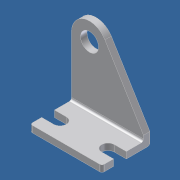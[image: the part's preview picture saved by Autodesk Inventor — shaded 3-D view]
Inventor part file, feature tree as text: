
AUTODESK INVENTOR PART (.ipt)
format: ipt  version: unknown  size: 245,760 bytes
history: native  units: in
note: dims shown in document units (in); Inventor stores cm internally (conversion verified against a paired STEP export)
features: other x147, extrude x8, sketch x8
ambient origin geometry x8: Origin, YZ Plane, XZ Plane, XY Plane, X Axis, Y Axis, Z Axis, Center Point
feature tree (163):
  extrude  "Extrusion1"  Depth=1.0in TaperAngle=0.0deg
  extrude  "Extrusion2"  Depth=0.1345in TaperAngle=0.0deg
  extrude  "Extrusion3"  Depth=0.1345in TaperAngle=0.0deg
  extrude  "Extrusion4"  Depth=0.1345in TaperAngle=0.0deg
  extrude  "Extrusion5"  [1 undecoded]
  sketch  "Sketch_6"
  sketch  "Sketch_7"
  extrude  "Extrusion6"  [1 undecoded]
  extrude  "Extrusion7"  [1 undecoded]
  extrude  "Extrusion8"  [1 undecoded]
  other  "a1_XY"
  other  "a1_YZ"
  other  "a1_ZX"
  other  "a1_X"
  other  "a1_Y"
  other  "a1_Z"
  other  "a1_Center"
  other  "a2_XY"
  other  "a2_YZ"
  other  "a2_ZX"
  other  "a2_X"
  other  "a2_Y"
  other  "a2_Z"
  other  "a2_Center"
  other  "b1_XY"
  other  "b1_YZ"
  other  "b1_ZX"
  other  "b1_X"
  other  "b1_Y"
  other  "b1_Z"
  other  "b1_Center"
  other  "b2_XY"
  other  "b2_YZ"
  other  "b2_ZX"
  other  "b2_X"
  other  "b2_Y"
  other  "b2_Z"
  other  "b2_Center"
  other  "d1_XY"
  other  "d1_YZ"
  other  "d1_ZX"
  other  "d1_X"
  other  "d1_Y"
  other  "d1_Z"
  other  "d1_Center"
  other  "d2_XY"
  other  "d2_YZ"
  other  "d2_ZX"
  other  "d2_X"
  other  "d2_Y"
  other  "d2_Z"
  other  "d2_Center"
  other  "e1_XY"
  other  "e1_YZ"
  other  "e1_ZX"
  other  "e1_X"
  other  "e1_Y"
  other  "e1_Z"
  other  "e1_Center"
  other  "e2_XY"
  other  "e2_YZ"
  other  "e2_ZX"
  other  "e2_X"
  other  "e2_Y"
  other  "e2_Z"
  other  "e2_Center"
  other  "f1_XY"
  other  "f1_YZ"
  other  "f1_ZX"
  other  "f1_X"
  other  "f1_Y"
  other  "f1_Z"
  other  "f1_Center"
  other  "f2_XY"
  other  "f2_YZ"
  other  "f2_ZX"
  other  "f2_X"
  other  "f2_Y"
  other  "f2_Z"
  other  "f2_Center"
  other  "g1_XY"
  other  "g1_YZ"
  other  "g1_ZX"
  other  "g1_X"
  other  "g1_Y"
  other  "g1_Z"
  other  "g1_Center"
  other  "g2_XY"
  other  "g2_YZ"
  other  "g2_ZX"
  other  "g2_X"
  other  "g2_Y"
  other  "g2_Z"
  other  "g2_Center"
  other  "h1_XY"
  other  "h1_YZ"
  other  "h1_ZX"
  other  "h1_X"
  other  "h1_Y"
  other  "h1_Z"
  other  "h1_Center"
  other  "h2_XY"
  other  "h2_YZ"
  other  "h2_ZX"
  other  "h2_X"
  other  "h2_Y"
  other  "h2_Z"
  other  "h2_Center"
  other  "i_XY"
  other  "i_YZ"
  other  "i_ZX"
  other  "i_X"
  other  "i_Y"
  other  "i_Z"
  other  "i_Center"
  other  "j1_XY"
  other  "j1_YZ"
  other  "j1_ZX"
  other  "j1_X"
  other  "j1_Y"
  other  "j1_Z"
  other  "j1_Center"
  other  "j2_XY"
  other  "j2_YZ"
  other  "j2_ZX"
  other  "j2_X"
  other  "j2_Y"
  other  "j2_Z"
  other  "j2_Center"
  other  "k11_XY"
  other  "k11_YZ"
  other  "k11_ZX"
  other  "k11_X"
  other  "k11_Y"
  other  "k11_Z"
  other  "k11_Center"
  other  "k12_XY"
  other  "k12_YZ"
  other  "k12_ZX"
  other  "k12_X"
  other  "k12_Y"
  other  "k12_Z"
  other  "k12_Center"
  other  "to_dummy_L_XY"
  other  "to_dummy_L_YZ"
  other  "to_dummy_L_ZX"
  other  "to_dummy_L_X"
  other  "to_dummy_L_Y"
  other  "to_dummy_L_Z"
  other  "to_dummy_L_Center"
  other  "to_pin_L_XY"
  other  "to_pin_L_YZ"
  other  "to_pin_L_ZX"
  other  "to_pin_L_X"
  other  "to_pin_L_Y"
  other  "to_pin_L_Z"
  other  "to_pin_L_Center"
  sketch  "Sketch_1"  dims[d0=1.5in d1=0.0in d2=1.0in d3=0.0in]
  sketch  "Sketch_2"  dims[d4=0.1345in d5=0.0in d6=0.1345in d7=0.0in]
  sketch  "Sketch_3"  dims[d8=0.1345in d9=0.0in d10=0.1345in d11=0.0in]
  sketch  "Sketch_4"  dims[d12=0.1345in d13=0.0in d14=0.1345in d15=0.0in]
  sketch  "Sketch_5"
  sketch  "Sketch_8"
note: 4 required parameter values undecoded (feature->parameter linkage not recoverable at this tier; creation-order binding heuristic only, values carry confidence <= 0.55)
